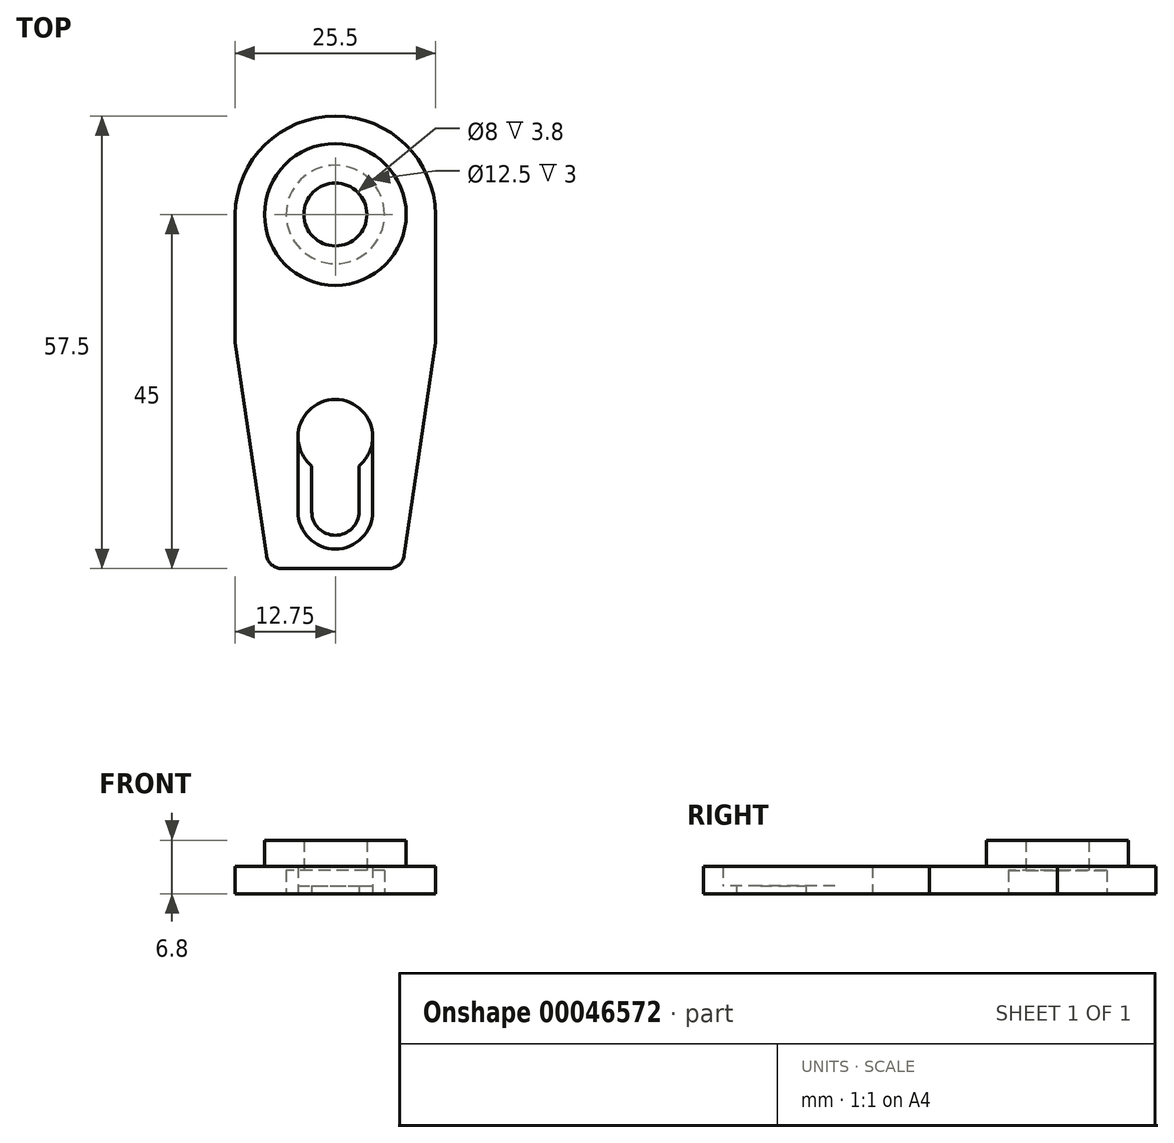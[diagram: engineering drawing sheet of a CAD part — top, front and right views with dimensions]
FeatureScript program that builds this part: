
annotation { "Feature Type Name" : "Feature", "Feature Type Description" : "" }
export const myFeature = defineFeature(function(context is Context, id is Id, definition is map)
    precondition{}
    {
        {
            var Q0;
            Q0=qCreatedBy(makeId("Top.planeOp"),FACE);
            var sketch = newSketch(context, id + "F0", { "sketchPlane" : qUnion([Q0])});
            skLineSegment(sketch, "E0.rect.top", {"start": v(-6.77, -28.75) * mm, "end": v(6.77, -28.75) * mm});
            skLineSegment(sketch, "E0.rect.left", {"start": v(-12.75, 16.25) * mm, "end": v(-12.75, 0) * mm});
            skLineSegment(sketch, "E0.rect.right", {"start": v(12.75, 16.25) * mm, "end": v(12.75, 0) * mm});
            skPoint(sketch, "E0.rect.middle", {"position": v(0, 0) * mm});
            skLineSegment(sketch, "E1", {"start": v(-12.75, 0) * mm, "end": v(-8.75, -27.04) * mm});
            skLineSegment(sketch, "E2", {"start": v(12.75, 0) * mm, "end": v(8.75, -27.04) * mm});
            skPoint(sketch, "E3.orphan", {"position": v(-12.75, -28.75) * mm});
            skPoint(sketch, "E4.orphan", {"position": v(12.75, -28.75) * mm});
            skPoint(sketch, "E5", {"position": v(0, -28.75) * mm});
            skCircle(sketch, "E6", {"center": v(0, 16.25) * mm, "radius": 9 * mm});
            skCircle(sketch, "E7", {"center": v(0, 16.25) * mm, "radius": 4 * mm});
            skCircle(sketch, "E8", {"center": v(0, 16.25) * mm, "radius": 6.25 * mm});
            skLineSegment(sketch, "E9.rect.left", {"start": v(-4.75, -12) * mm, "end": v(-4.75, -21.5) * mm});
            skLineSegment(sketch, "E9.rect.right", {"start": v(4.75, -12) * mm, "end": v(4.75, -21.5) * mm});
            skPoint(sketch, "E9.rect.middle", {"position": v(0, -16.75) * mm});
            skArc(sketch, "E10", {"start": v(-4.75, -12) * mm, "mid": v(0, -7.25) * mm, "end": v(4.75, -12) * mm});
            skArc(sketch, "E11", {"start": v(-4.75, -21.5) * mm, "mid": v(0, -26.25) * mm, "end": v(4.75, -21.5) * mm});
            skLineSegment(sketch, "E12.rect.left", {"start": v(-3, -21.5) * mm, "end": v(-3, -15.68) * mm});
            skLineSegment(sketch, "E12.rect.right", {"start": v(3, -21.5) * mm, "end": v(3, -15.68) * mm});
            skArc(sketch, "E13", {"start": v(-3, -21.5) * mm, "mid": v(0, -24.5) * mm, "end": v(3, -21.5) * mm});
            skArc(sketch, "E14", {"start": v(-4.75, -12) * mm, "mid": v(-4.3, -14.04) * mm, "end": v(-3, -15.68) * mm});
            skArc(sketch, "E15", {"start": v(4.75, -12) * mm, "mid": v(4.3, -14.04) * mm, "end": v(3, -15.68) * mm});
            skPoint(sketch, "E16.orphan", {"position": v(3, -12) * mm});
            skPoint(sketch, "E12.rect.top.start.orphan", {"position": v(-3, -12) * mm});
            skArc(sketch, "E17", {"start": v(12.75, 16.25) * mm, "mid": v(0, 28.75) * mm, "end": v(-12.75, 16.25) * mm});
            skPoint(sketch, "E18", {"position": v(0, 28.75) * mm});
            skPoint(sketch, "E19.orphan", {"position": v(-12.75, 28.75) * mm});
            skPoint(sketch, "E20.orphan", {"position": v(12.75, 28.75) * mm});
            skPoint(sketch, "E21.start.orphan", {"position": v(-25.88, 0) * mm});
            skPoint(sketch, "E22.orphan", {"position": v(0, 44.52) * mm});
            skPoint(sketch, "E23.visualSharp", {"position": v(8.5, -28.75) * mm});
            skArc(sketch, "E23.filletArc", {"start": v(6.77, -28.75) * mm, "mid": v(8.08, -28.26) * mm, "end": v(8.75, -27.04) * mm});
            skPoint(sketch, "E24.visualSharp", {"position": v(-8.5, -28.75) * mm});
            skArc(sketch, "E24.filletArc", {"start": v(-8.75, -27.04) * mm, "mid": v(-8.08, -28.26) * mm, "end": v(-6.77, -28.75) * mm});
            skSolve(sketch);
        }
        {
            var Q0;
            Q0 = qSketchRegion(id + "F0", true);
            var Q1;
            Q1=makeQuery(id+"F0.imprint","IMPRINT",FACE,{"disambiguationData":[TD([[makeQuery(id+"F0.imprint","IMPRINT",EDGE,{"derivedFrom":sQuery(id+"F0.wireOp",EDGE,"E0.rect.top")}),1.0]])]});
            extrude(context, id + "F1", {"entities" : qUnion([Q0, Q1]), "depth" : 3.5 * mm});
        }
        {
            var Q0;
            Q0=makeQuery(id+"F0.imprint","IMPRINT",FACE,{"disambiguationData":[TD([[makeQuery(id+"F0.imprint","IMPRINT",EDGE,{"derivedFrom":sQuery(id+"F0.wireOp",EDGE,"E9.rect.left")}),1.0]])]});
            extrude(context, id + "F2", {"entities" : qUnion([Q0]), "operationType" : NewBodyOperationType.ADD, "depth" : 1 * mm});
        }
        {
            var Q0;
            Q0=makeQuery(id+"F0.imprint","IMPRINT",FACE,{"disambiguationData":[TD([[makeQuery(id+"F0.imprint","IMPRINT",EDGE,{"derivedFrom":sQuery(id+"F0.wireOp",EDGE,"E6")}),1.0]])]});
            var Q1;
            Q1=makeQuery(id+"F0.imprint","IMPRINT",FACE,{"disambiguationData":[TD([[makeQuery(id+"F0.imprint","IMPRINT",EDGE,{"derivedFrom":sQuery(id+"F0.wireOp",EDGE,"E7")}),-1.0]])]});
            extrude(context, id + "F3", {"entities" : qUnion([Q0, Q1]), "operationType" : NewBodyOperationType.ADD, "depth" : 6.8 * mm});
        }
        {
            var Q0;
            Q0=makeQuery(id+"F0.imprint","IMPRINT",FACE,{"disambiguationData":[TD([[makeQuery(id+"F0.imprint","IMPRINT",EDGE,{"derivedFrom":sQuery(id+"F0.wireOp",EDGE,"E7")}),-1.0]])]});
            extrude(context, id + "F4", {"entities" : qUnion([Q0]), "operationType" : NewBodyOperationType.REMOVE, "depth" : 3 * mm});
        }
    });
